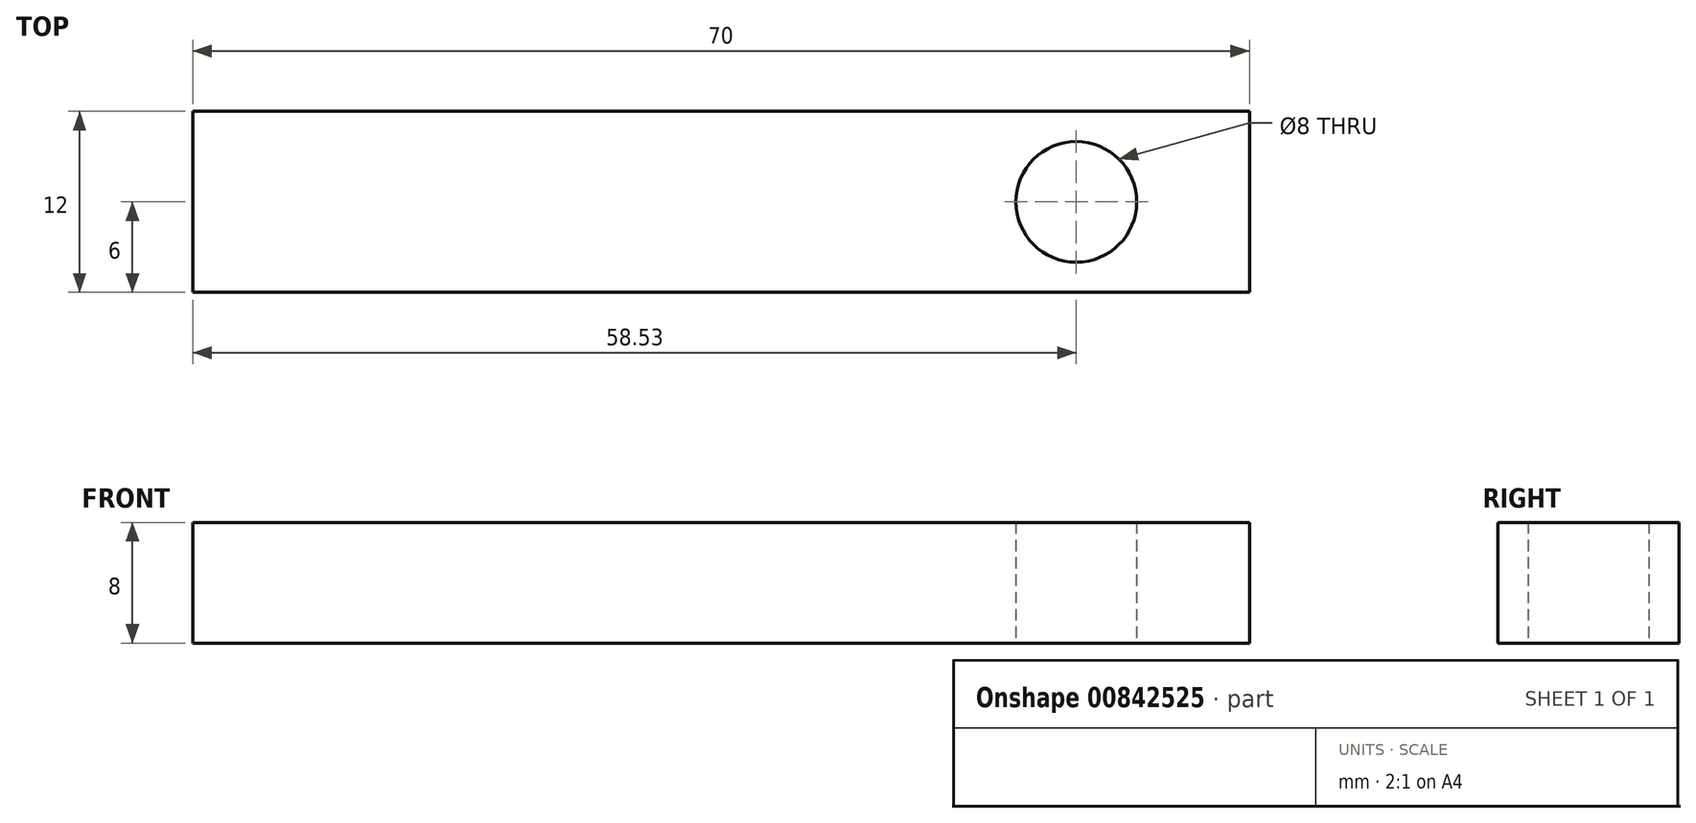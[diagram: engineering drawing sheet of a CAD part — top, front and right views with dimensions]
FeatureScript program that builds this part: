
annotation { "Feature Type Name" : "Feature", "Feature Type Description" : "" }
export const myFeature = defineFeature(function(context is Context, id is Id, definition is map)
    precondition{}
    {
        {
            var Q0;
            Q0=qCreatedBy(makeId("Top.planeOp"),FACE);
            var sketch = newSketch(context, id + "F0", { "sketchPlane" : qUnion([Q0])});
            skLineSegment(sketch, "E0.bottom", {"start": v(0, 0) * mm, "end": v(-70, 0) * mm});
            skLineSegment(sketch, "E0.top", {"start": v(0, -12) * mm, "end": v(-70, -12) * mm});
            skLineSegment(sketch, "E0.left", {"start": v(0, 0) * mm, "end": v(0, -12) * mm});
            skLineSegment(sketch, "E0.right", {"start": v(-70, 0) * mm, "end": v(-70, -12) * mm});
            skCircle(sketch, "E1", {"center": v(-11.47, -6) * mm, "radius": 4 * mm});
            skPoint(sketch, "E1.centerSnap0", {"position": v(0, -6) * mm});
            skSolve(sketch);
        }
        {
            var Q0;
            Q0 = qSketchRegion(id + "F0", true);
            extrude(context, id + "F1", {"entities" : qUnion([Q0]), "depth" : 8 * mm, "offsetDistance" : 25 * mm});
        }
    });
